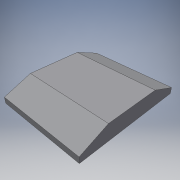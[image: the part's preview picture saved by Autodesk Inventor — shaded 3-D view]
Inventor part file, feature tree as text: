
AUTODESK INVENTOR PART (.ipt)
format: ipt  version: 2016 (Build 200138000, 138)  size: 101,376 bytes
history: native  units: in
note: dims shown in document units (in); Inventor stores cm internally (conversion verified against a paired STEP export)
features: extrude x2, sketch x2
ambient origin geometry x8: Origin, YZ Plane, XZ Plane, XY Plane, X Axis, Y Axis, Z Axis, Center Point
bodies: Solid1 (feature_tree)
feature tree (4):
  extrude  "Extrusion1"  Depth=13.3in
  extrude  "Extrusion2"  Depth=2.56in
  sketch  "Sketch1"  dims[d0=16.2in d1=13.3in]
  sketch  "Sketch2"  dims[d2=2.56in d3=0.0in d4=8.1in d5=0.94in d6=0.94in d7=15.2475in d8=0.0in]
